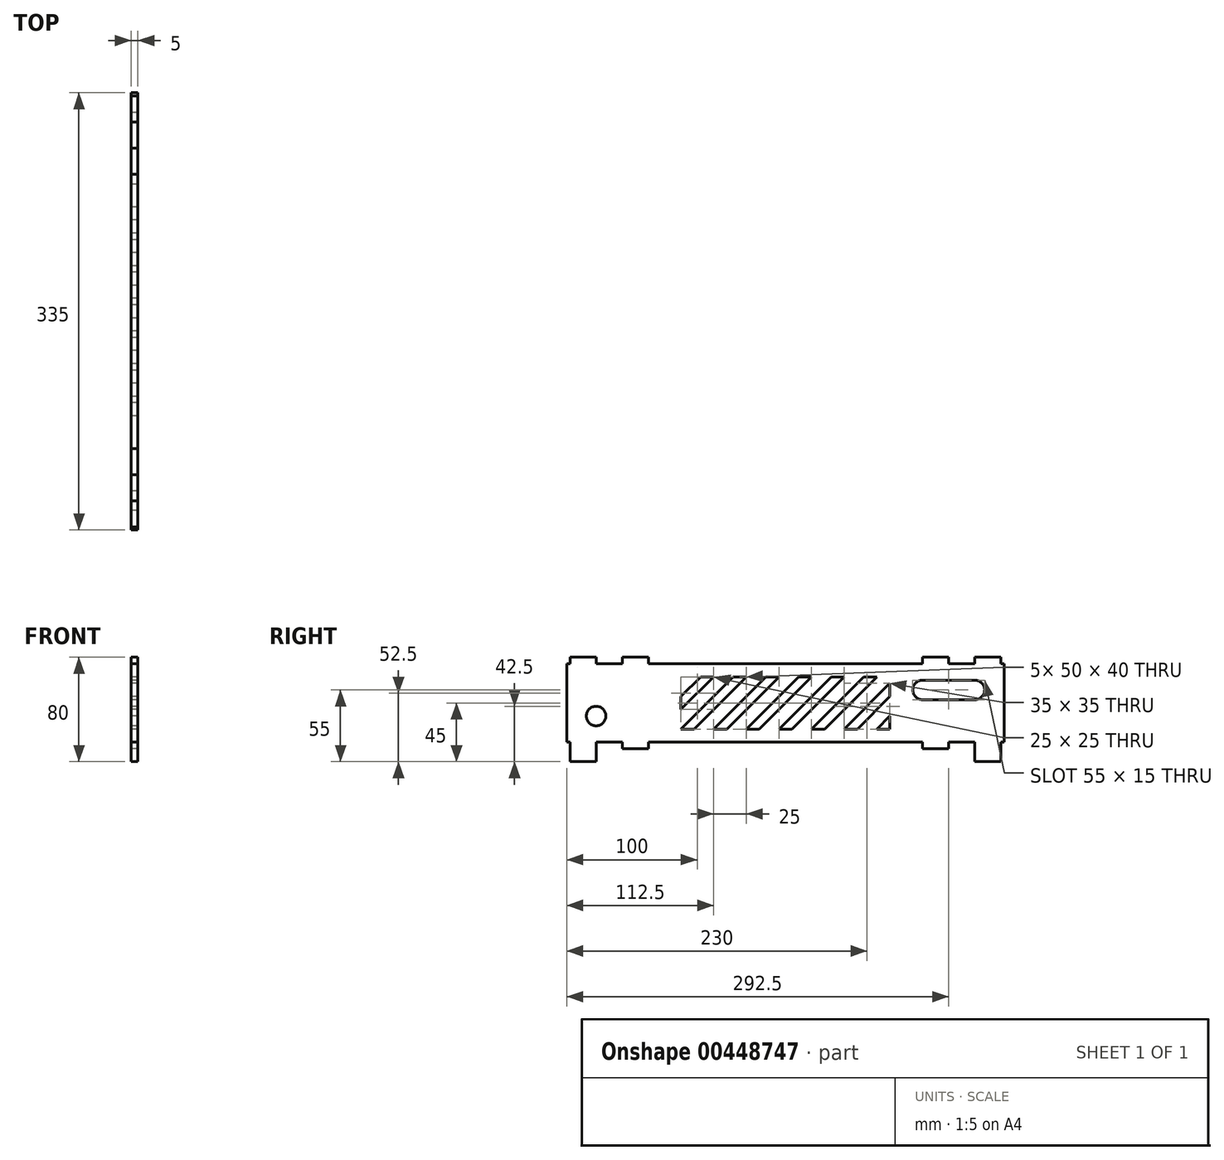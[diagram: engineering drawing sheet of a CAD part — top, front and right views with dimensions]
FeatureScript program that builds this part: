
annotation { "Feature Type Name" : "Feature", "Feature Type Description" : "" }
export const myFeature = defineFeature(function(context is Context, id is Id, definition is map)
    precondition{}
    {
        {
            assignVariable(context, id + "F0", {"name" : "thickness", "anyValue" : 5 * mm});
        }
        {
            var Q0;
            Q0=qCreatedBy(makeId("Right.planeOp"),FACE);
            var sketch = newSketch(context, id + "F1", { "sketchPlane" : qUnion([Q0])});
            skLineSegment(sketch, "E0.bottom", {"start": v(0, 0) * mm, "end": v(335, 0) * mm});
            skLineSegment(sketch, "E0.top", {"start": v(0, 60) * mm, "end": v(335, 60) * mm});
            skLineSegment(sketch, "E0.left", {"start": v(0, 0) * mm, "end": v(0, 60) * mm});
            skLineSegment(sketch, "E0.right", {"start": v(335, 0) * mm, "end": v(335, 60) * mm});
            skLineSegment(sketch, "E1", {"start": v(332.5, 0) * mm, "end": v(332.5, -15) * mm});
            skLineSegment(sketch, "E2", {"start": v(332.5, -15) * mm, "end": v(312.5, -15) * mm});
            skLineSegment(sketch, "E3", {"start": v(312.5, -15) * mm, "end": v(312.5, 0) * mm});
            skLineSegment(sketch, "E4", {"start": v(292.5, 0) * mm, "end": v(292.5, -5) * mm});
            skLineSegment(sketch, "E5", {"start": v(292.5, -5) * mm, "end": v(272.5, -5) * mm});
            skLineSegment(sketch, "E6", {"start": v(272.5, -5) * mm, "end": v(272.5, 0) * mm});
            skLineSegment(sketch, "E7", {"start": v(167.5, 60) * mm, "end": v(167.5, 0) * mm, "construction": true});
            skLineSegment(sketch, "E8", {"start": v(0, 30) * mm, "end": v(335, 30) * mm, "construction": true});
            skLineSegment(sketch, "E9.MirrorCS", {"start": v(62.5, -5) * mm, "end": v(62.5, 0) * mm});
            skLineSegment(sketch, "E10.MirrorCS", {"start": v(42.5, 0) * mm, "end": v(42.5, -5) * mm});
            skLineSegment(sketch, "E11.MirrorCS", {"start": v(42.5, -5) * mm, "end": v(62.5, -5) * mm});
            skLineSegment(sketch, "E12.MirrorCS", {"start": v(2.5, 0) * mm, "end": v(2.5, -15) * mm});
            skLineSegment(sketch, "E13.MirrorCS", {"start": v(2.5, -15) * mm, "end": v(22.5, -15) * mm});
            skLineSegment(sketch, "E14.MirrorCS", {"start": v(22.5, -15) * mm, "end": v(22.5, 0) * mm});
            skLineSegment(sketch, "E15.MirrorCS", {"start": v(62.5, 65) * mm, "end": v(62.5, 60) * mm});
            skLineSegment(sketch, "E16.MirrorCS", {"start": v(42.5, 60) * mm, "end": v(42.5, 65) * mm});
            skLineSegment(sketch, "E17.MirrorCS", {"start": v(42.5, 65) * mm, "end": v(62.5, 65) * mm});
            skLineSegment(sketch, "E18.MirrorCS", {"start": v(272.5, 65) * mm, "end": v(272.5, 60) * mm});
            skLineSegment(sketch, "E19.MirrorCS", {"start": v(292.5, 60) * mm, "end": v(292.5, 65) * mm});
            skLineSegment(sketch, "E20.MirrorCS", {"start": v(292.5, 65) * mm, "end": v(272.5, 65) * mm});
            skLineSegment(sketch, "E21", {"start": v(2.5, 60) * mm, "end": v(2.5, 65) * mm});
            skLineSegment(sketch, "E22", {"start": v(2.5, 65) * mm, "end": v(22.5, 65) * mm});
            skLineSegment(sketch, "E23", {"start": v(22.5, 65) * mm, "end": v(22.5, 60) * mm});
            skLineSegment(sketch, "E24.MirrorCS", {"start": v(332.5, 65) * mm, "end": v(312.5, 65) * mm});
            skLineSegment(sketch, "E25.MirrorCS", {"start": v(312.5, 65) * mm, "end": v(312.5, 60) * mm});
            skLineSegment(sketch, "E26.MirrorCS", {"start": v(332.5, 60) * mm, "end": v(332.5, 65) * mm});
            skLineSegment(sketch, "E27", {"start": v(272.5, 40) * mm, "end": v(312.5, 40) * mm, "construction": true});
            skArc(sketch, "E28.0.startCap", {"start": v(272.5, 32.5) * mm, "mid": v(265, 40) * mm, "end": v(272.5, 47.5) * mm});
            skArc(sketch, "E28.0.endCap", {"start": v(312.5, 47.5) * mm, "mid": v(320, 40) * mm, "end": v(312.5, 32.5) * mm});
            skLineSegment(sketch, "E28.0.left", {"start": v(272.5, 47.5) * mm, "end": v(312.5, 47.5) * mm});
            skLineSegment(sketch, "E28.0.right", {"start": v(272.5, 32.5) * mm, "end": v(312.5, 32.5) * mm});
            skCircle(sketch, "E29", {"center": v(22.5, 20) * mm, "radius": 7.5 * mm});
            skLineSegment(sketch, "E30.bottom", {"start": v(87.5, 50) * mm, "end": v(247.5, 50) * mm, "construction": true});
            skLineSegment(sketch, "E30.top", {"start": v(87.5, 10) * mm, "end": v(247.5, 10) * mm, "construction": true});
            skLineSegment(sketch, "E30.left", {"start": v(87.5, 50) * mm, "end": v(87.5, 10) * mm, "construction": true});
            skLineSegment(sketch, "E30.right", {"start": v(247.5, 50) * mm, "end": v(247.5, 10) * mm, "construction": true});
            skPoint(sketch, "E31", {"position": v(167.5, 50) * mm});
            skPoint(sketch, "E32", {"position": v(87.5, 30) * mm});
            skLineSegment(sketch, "E33", {"start": v(87.5, 10) * mm, "end": v(127.5, 50) * mm});
            skLineSegment(sketch, "E34", {"start": v(127.5, 50) * mm, "end": v(137.5, 50) * mm});
            skLineSegment(sketch, "E35", {"start": v(137.5, 50) * mm, "end": v(97.5, 10) * mm});
            skLineSegment(sketch, "E36", {"start": v(97.5, 10) * mm, "end": v(87.5, 10) * mm});
            skLineSegment(sketch, "E37.1.0.0", {"start": v(112.5, 10) * mm, "end": v(152.5, 50) * mm});
            skLineSegment(sketch, "E37.1.0.1", {"start": v(162.5, 50) * mm, "end": v(122.5, 10) * mm});
            skLineSegment(sketch, "E37.1.0.2", {"start": v(152.5, 50) * mm, "end": v(162.5, 50) * mm});
            skLineSegment(sketch, "E37.1.0.3", {"start": v(122.5, 10) * mm, "end": v(112.5, 10) * mm});
            skLineSegment(sketch, "E37.2.0.0", {"start": v(137.5, 10) * mm, "end": v(177.5, 50) * mm});
            skLineSegment(sketch, "E37.2.0.1", {"start": v(187.5, 50) * mm, "end": v(147.5, 10) * mm});
            skLineSegment(sketch, "E37.2.0.2", {"start": v(177.5, 50) * mm, "end": v(187.5, 50) * mm});
            skLineSegment(sketch, "E37.2.0.3", {"start": v(147.5, 10) * mm, "end": v(137.5, 10) * mm});
            skLineSegment(sketch, "E37.3.0.0", {"start": v(162.5, 10) * mm, "end": v(202.5, 50) * mm});
            skLineSegment(sketch, "E37.3.0.1", {"start": v(212.5, 50) * mm, "end": v(172.5, 10) * mm});
            skLineSegment(sketch, "E37.3.0.2", {"start": v(202.5, 50) * mm, "end": v(212.5, 50) * mm});
            skLineSegment(sketch, "E37.3.0.3", {"start": v(172.5, 10) * mm, "end": v(162.5, 10) * mm});
            skLineSegment(sketch, "E37.4.0.0", {"start": v(187.5, 10) * mm, "end": v(227.5, 50) * mm});
            skLineSegment(sketch, "E37.4.0.1", {"start": v(237.5, 50) * mm, "end": v(197.5, 10) * mm});
            skLineSegment(sketch, "E37.4.0.2", {"start": v(227.5, 50) * mm, "end": v(237.5, 50) * mm});
            skLineSegment(sketch, "E37.4.0.3", {"start": v(197.5, 10) * mm, "end": v(187.5, 10) * mm});
            skLineSegment(sketch, "E37.5.0.0", {"start": v(212.5, 10) * mm, "end": v(247.5, 45) * mm});
            skLineSegment(sketch, "E37.5.0.1", {"start": v(247.5, 35) * mm, "end": v(222.5, 10) * mm});
            skLineSegment(sketch, "E37.5.0.3", {"start": v(222.5, 10) * mm, "end": v(212.5, 10) * mm});
            skLineSegment(sketch, "E37.6.0.0", {"start": v(237.5, 10) * mm, "end": v(247.5, 20) * mm});
            skLineSegment(sketch, "E37.6.0.3", {"start": v(247.5, 10) * mm, "end": v(237.5, 10) * mm});
            skLineSegment(sketch, "E37.direction1", {"start": v(87.5, 10) * mm, "end": v(112.5, 10) * mm, "construction": true});
            skLineSegment(sketch, "E38.1.0.1", {"start": v(112.5, 50) * mm, "end": v(87.5, 25) * mm});
            skLineSegment(sketch, "E38.1.0.2", {"start": v(102.5, 50) * mm, "end": v(112.5, 50) * mm});
            skLineSegment(sketch, "E38.direction1", {"start": v(87.5, 10) * mm, "end": v(62.5, 10) * mm, "construction": true});
            skLineSegment(sketch, "E39.trimOffspring", {"start": v(87.5, 35) * mm, "end": v(102.5, 50) * mm});
            skLineSegment(sketch, "E40", {"start": v(87.5, 35) * mm, "end": v(87.5, 25) * mm});
            skLineSegment(sketch, "E41", {"start": v(247.5, 45) * mm, "end": v(247.5, 35) * mm});
            skLineSegment(sketch, "E42", {"start": v(247.5, 20) * mm, "end": v(247.5, 10) * mm});
            skSolve(sketch);
        }
        {
            var Q0;
            Q0=qSketchRegion(id+"F1",true);
            extrude(context, id + "F2", {"entities" : qUnion([Q0]), "depth" : getVariable(context, 'thickness')});
        }
    });
